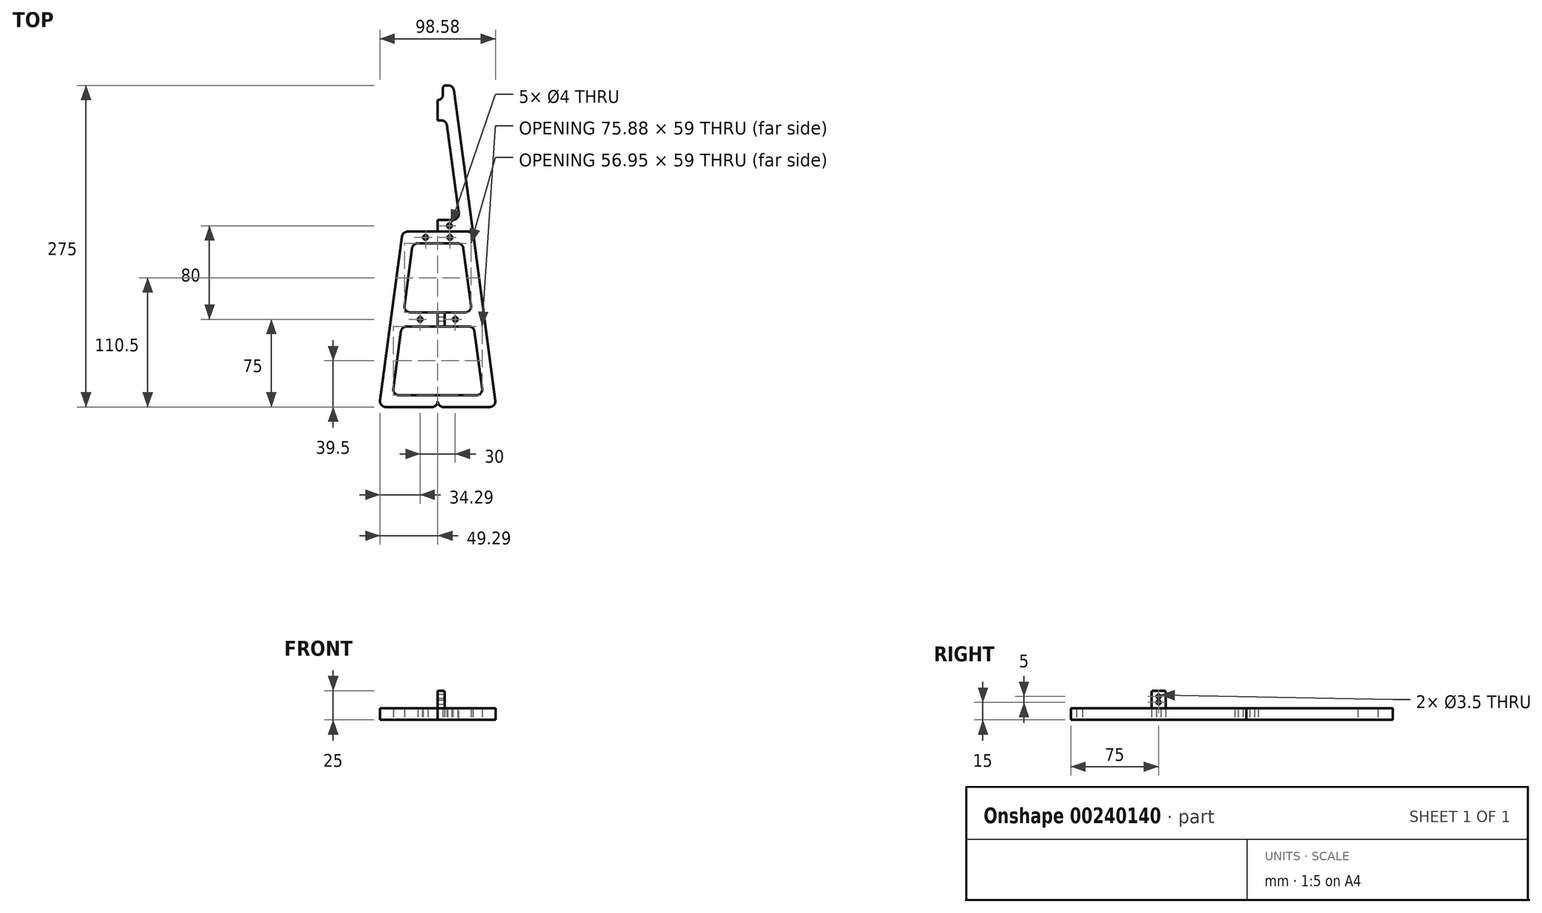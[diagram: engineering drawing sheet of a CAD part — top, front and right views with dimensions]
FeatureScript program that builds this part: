
annotation { "Feature Type Name" : "Feature", "Feature Type Description" : "" }
export const myFeature = defineFeature(function(context is Context, id is Id, definition is map)
    precondition{}
    {
        {
            var Q0;
            Q0=qCreatedBy(makeId("Top.planeOp"),FACE);
            var sketch = newSketch(context, id + "F0", { "sketchPlane" : qUnion([Q0])});
            skLineSegment(sketch, "E0.top", {"start": v(0, 75) * mm, "end": v(-30, 75) * mm});
            skPoint(sketch, "E0.middle", {"position": v(0, 0) * mm});
            skLineSegment(sketch, "E1", {"start": v(-30, 75) * mm, "end": v(-50, -75) * mm});
            skPoint(sketch, "E0.right.end.orphan", {"position": v(-50, 75) * mm});
            skPoint(sketch, "E0.left.end.orphan", {"position": v(50, 75) * mm});
            skLineSegment(sketch, "E2", {"start": v(0, 0) * mm, "end": v(0, 6) * mm});
            skLineSegment(sketch, "E3", {"start": v(-50, -75) * mm, "end": v(-40, -75) * mm});
            skLineSegment(sketch, "E4", {"start": v(-30, 75) * mm, "end": v(-20, 75) * mm});
            skLineSegment(sketch, "E5", {"start": v(0, 75) * mm, "end": v(0, 65) * mm});
            skLineSegment(sketch, "E6", {"start": v(0, 65) * mm, "end": v(-21.33, 65) * mm});
            skLineSegment(sketch, "E7", {"start": v(0, -75) * mm, "end": v(0, -65) * mm});
            skLineSegment(sketch, "E8", {"start": v(0, -65) * mm, "end": v(-38.67, -65) * mm});
            skLineSegment(sketch, "E9", {"start": v(0, 6) * mm, "end": v(-29.2, 6) * mm});
            skLineSegment(sketch, "E10", {"start": v(0, 0) * mm, "end": v(0, -6) * mm});
            skLineSegment(sketch, "E11", {"start": v(0, -6) * mm, "end": v(-30.8, -6) * mm});
            skLineSegment(sketch, "E12.trimOffspring", {"start": v(-30.8, -6) * mm, "end": v(-38.67, -65) * mm});
            skLineSegment(sketch, "E13", {"start": v(-21.33, 65) * mm, "end": v(-29.2, 6) * mm});
            skLineSegment(sketch, "E14.trimOffspring", {"start": v(0, -75) * mm, "end": v(-50, -75) * mm});
            skPoint(sketch, "E0.bottom.start.orphan", {"position": v(50, -75) * mm});
            skCircle(sketch, "E15", {"center": v(-15, 0) * mm, "radius": 2 * mm});
            skLineSegment(sketch, "E16", {"start": v(0, 65) * mm, "end": v(0, 70) * mm});
            skCircle(sketch, "E17", {"center": v(-10.41, 70) * mm, "radius": 2 * mm});
            skSolve(sketch);
        }
        {
            var Q0;
            Q0=qSketchRegion(id+"F0",true);
            extrude(context, id + "F1", {"entities" : qUnion([Q0]), "depth" : 10 * mm});
        }
        {
            var Q0;
            Q0=makeQuery(id+"F1.opExtrude","SWEPT_EDGE",EDGE,{"disambiguationData":[OSD([sQuery(id+"F0.wireOp",EDGE,"E6"),sQuery(id+"F0.wireOp",EDGE,"E13")])]});
            var Q1;
            Q1=makeQuery(id+"F1.opExtrude","SWEPT_EDGE",EDGE,{"disambiguationData":[OSD([sQuery(id+"F0.wireOp",EDGE,"E11"),sQuery(id+"F0.wireOp",EDGE,"E12.trimOffspring")])]});
            var Q2;
            Q2=makeQuery(id+"F1.opExtrude","SWEPT_EDGE",EDGE,{"disambiguationData":[OSD([sQuery(id+"F0.wireOp",EDGE,"E9"),sQuery(id+"F0.wireOp",EDGE,"E13")])]});
            var Q3;
            Q3=makeQuery(id+"F1.opExtrude","SWEPT_EDGE",EDGE,{"disambiguationData":[OSD([sQuery(id+"F0.wireOp",EDGE,"E8"),sQuery(id+"F0.wireOp",EDGE,"E12.trimOffspring")])]});
            var Q4;
            Q4=makeQuery(id+"F1.opExtrude","SWEPT_EDGE",EDGE,{"disambiguationData":[OSD([sQuery(id+"F0.wireOp",EDGE,"E1"),sQuery(id+"F0.wireOp",EDGE,"E14.trimOffspring")])]});
            fillet(context, id + "F2", {"entities" : qUnion([Q0, Q1, Q2, Q3, Q4]), "radius" : 5 * mm, "tangentPropagation" : true, "allowEdgeOverflow" : false});
        }
        {
            var Q0;
            Q0=makeQuery(id+"F1.opExtrude","SWEPT_BODY",BODY,{"disambiguationData":[OSD([sQuery(id+"F0.wireOp",EDGE,"E0.top"),sQuery(id+"F0.wireOp",EDGE,"E1"),sQuery(id+"F0.wireOp",EDGE,"E2"),sQuery(id+"F0.wireOp",EDGE,"E4"),sQuery(id+"F0.wireOp",EDGE,"E5"),sQuery(id+"F0.wireOp",EDGE,"E6"),sQuery(id+"F0.wireOp",EDGE,"E7"),sQuery(id+"F0.wireOp",EDGE,"E8"),sQuery(id+"F0.wireOp",EDGE,"E9"),sQuery(id+"F0.wireOp",EDGE,"E10"),sQuery(id+"F0.wireOp",EDGE,"E11"),sQuery(id+"F0.wireOp",EDGE,"E12.trimOffspring"),sQuery(id+"F0.wireOp",EDGE,"E13"),sQuery(id+"F0.wireOp",EDGE,"E14.trimOffspring"),sQuery(id+"F0.wireOp",EDGE,"E15"),sQuery(id+"F0.wireOp",EDGE,"E16"),sQuery(id+"F0.wireOp",EDGE,"E17")])]});
            var Q1;
            Q1=qCreatedBy(makeId("Right.planeOp"),FACE);
            mirror(context, id + "F3", {"operationType" : NewBodyOperationType.ADD, "entities" : qUnion([Q0]), "mirrorPlane" : qUnion([Q1])});
        }
        {
            var Q0;
            Q0=qCreatedBy(makeId("Top.planeOp"),FACE);
            var sketch = newSketch(context, id + "F4", { "sketchPlane" : qUnion([Q0])});
            skLineSegment(sketch, "E18", {"start": v(0, 0) * mm, "end": v(40, 0) * mm});
            skLineSegment(sketch, "E19", {"start": v(0, 75) * mm, "end": v(30, 75) * mm});
            skLineSegment(sketch, "E20", {"start": v(0, 75) * mm, "end": v(0, 85) * mm});
            skLineSegment(sketch, "E21", {"start": v(4.5, 200) * mm, "end": v(13.33, 200) * mm});
            skLineSegment(sketch, "E22", {"start": v(30, 75) * mm, "end": v(13.33, 200) * mm});
            skArc(sketch, "E23", {"start": v(0, 187.5) * mm, "mid": v(3.18, 188.82) * mm, "end": v(4.5, 192) * mm});
            skLineSegment(sketch, "E24", {"start": v(4.5, 200) * mm, "end": v(4.5, 192) * mm});
            skLineSegment(sketch, "E25", {"start": v(0, 75) * mm, "end": v(0, 80) * mm});
            skCircle(sketch, "E26", {"center": v(10, 80) * mm, "radius": 2 * mm});
            skLineSegment(sketch, "E27", {"start": v(0, 75) * mm, "end": v(10, 75) * mm});
            skLineSegment(sketch, "E28", {"start": v(10, 85) * mm, "end": v(18.67, 85) * mm});
            skLineSegment(sketch, "E29", {"start": v(18.67, 85) * mm, "end": v(10, 150) * mm});
            skLineSegment(sketch, "E30", {"start": v(10, 85) * mm, "end": v(0, 85) * mm});
            skLineSegment(sketch, "E31", {"start": v(18.67, 85) * mm, "end": v(7.31, 170.17) * mm});
            skLineSegment(sketch, "E32", {"start": v(7.31, 170.17) * mm, "end": v(0, 170.17) * mm});
            skLineSegment(sketch, "E33.trimOffspring", {"start": v(0, 170.17) * mm, "end": v(0, 187.5) * mm});
            skSolve(sketch);
        }
        {
            var Q0;
            Q0=qSketchRegion(id+"F4",true);
            extrude(context, id + "F5", {"entities" : qUnion([Q0]), "depth" : 10 * mm});
        }
        {
            var Q0;
            Q0=makeQuery(id+"F5.opExtrude","SWEPT_BODY",BODY,{"disambiguationData":[OSD([sQuery(id+"F4.wireOp",EDGE,"E19"),sQuery(id+"F4.wireOp",EDGE,"E20"),sQuery(id+"F4.wireOp",EDGE,"E21"),sQuery(id+"F4.wireOp",EDGE,"E22"),sQuery(id+"F4.wireOp",EDGE,"E23"),sQuery(id+"F4.wireOp",EDGE,"E24"),sQuery(id+"F4.wireOp",EDGE,"E25"),sQuery(id+"F4.wireOp",EDGE,"E26"),sQuery(id+"F4.wireOp",EDGE,"E27"),sQuery(id+"F4.wireOp",EDGE,"E28"),sQuery(id+"F4.wireOp",EDGE,"E30"),sQuery(id+"F4.wireOp",EDGE,"E31"),sQuery(id+"F4.wireOp",EDGE,"E32"),sQuery(id+"F4.wireOp",EDGE,"E33.trimOffspring")])]});
            var Q1;
            Q1=qCreatedBy(makeId("Right.planeOp"),FACE);
            mirror(context, id + "F6", {"entities" : qUnion([Q0]), "mirrorPlane" : qUnion([Q1])});
        }
        {
            var Q0;
            Q0=makeQuery(id+"F6.opPattern","COPY",EDGE,{"derivedFrom":makeQuery(id+"F5.opExtrude","SWEPT_EDGE",EDGE,{"disambiguationData":[OSD([sQuery(id+"F4.wireOp",EDGE,"E31"),sQuery(id+"F4.wireOp",EDGE,"E32")])]}),"instanceName":"1"});
            var Q1;
            Q1=makeQuery(id+"F5.opExtrude","SWEPT_EDGE",EDGE,{"disambiguationData":[OSD([sQuery(id+"F4.wireOp",EDGE,"E31"),sQuery(id+"F4.wireOp",EDGE,"E32")])]});
            var Q2;
            Q2=makeQuery(id+"F6.opPattern","COPY",EDGE,{"derivedFrom":makeQuery(id+"F5.opExtrude","SWEPT_EDGE",EDGE,{"disambiguationData":[OSD([sQuery(id+"F4.wireOp",EDGE,"E28"),sQuery(id+"F4.wireOp",EDGE,"E31")])]}),"instanceName":"1"});
            var Q3;
            Q3=makeQuery(id+"F5.opExtrude","SWEPT_EDGE",EDGE,{"disambiguationData":[OSD([sQuery(id+"F4.wireOp",EDGE,"E28"),sQuery(id+"F4.wireOp",EDGE,"E31")])]});
            var Q4;
            Q4=makeQuery(id+"F6.opPattern","COPY",EDGE,{"derivedFrom":makeQuery(id+"F5.opExtrude","SWEPT_EDGE",EDGE,{"disambiguationData":[OSD([sQuery(id+"F4.wireOp",EDGE,"E21"),sQuery(id+"F4.wireOp",EDGE,"E22")])]}),"instanceName":"1"});
            var Q5;
            Q5=makeQuery(id+"F5.opExtrude","SWEPT_EDGE",EDGE,{"disambiguationData":[OSD([sQuery(id+"F4.wireOp",EDGE,"E21"),sQuery(id+"F4.wireOp",EDGE,"E22")])]});
            fillet(context, id + "F7", {"entities" : qUnion([Q0, Q1, Q2, Q3, Q4, Q5]), "radius" : 5 * mm, "tangentPropagation" : true, "allowEdgeOverflow" : false});
        }
        {
            var Q0;
            Q0=makeQuery(id+"F5.opExtrude","SWEPT_EDGE",EDGE,{"disambiguationData":[OSD([sQuery(id+"F4.wireOp",EDGE,"E21"),sQuery(id+"F4.wireOp",EDGE,"E24")])]});
            var Q1;
            Q1=makeQuery(id+"F6.opPattern","COPY",EDGE,{"derivedFrom":makeQuery(id+"F5.opExtrude","SWEPT_EDGE",EDGE,{"disambiguationData":[OSD([sQuery(id+"F4.wireOp",EDGE,"E21"),sQuery(id+"F4.wireOp",EDGE,"E24")])]}),"instanceName":"1"});
            fillet(context, id + "F8", {"entities" : qUnion([Q0, Q1]), "radius" : 2 * mm, "tangentPropagation" : true, "allowEdgeOverflow" : false});
        }
        {
            var Q0;
            Q0=qCreatedBy(makeId("Top.planeOp"),FACE);
            var sketch = newSketch(context, id + "F9", { "sketchPlane" : qUnion([Q0])});
            skLineSegment(sketch, "E34", {"start": v(0, 0) * mm, "end": v(0, 6) * mm});
            skLineSegment(sketch, "E35", {"start": v(0, 6) * mm, "end": v(-6, 6) * mm});
            skLineSegment(sketch, "E36", {"start": v(-6, 6) * mm, "end": v(-6, -6) * mm});
            skLineSegment(sketch, "E37", {"start": v(-6, -6) * mm, "end": v(0, -6) * mm});
            skLineSegment(sketch, "E38", {"start": v(0, -6) * mm, "end": v(0, 0) * mm});
            skSolve(sketch);
        }
        {
            var Q0;
            Q0=qSketchRegion(id+"F9",true);
            extrude(context, id + "F10", {"entities" : qUnion([Q0]), "operationType" : NewBodyOperationType.ADD, "depth" : 25 * mm});
        }
        {
            var Q0;
            Q0=makeQuery(id+"F10.opExtrude","SWEPT_EDGE",EDGE,{"disambiguationData":[OSD([sQuery(id+"F9.wireOp",EDGE,"E36"),sQuery(id+"F9.wireOp",EDGE,"E37")])]});
            var Q1;
            Q1=makeQuery(id+"F10.opExtrude","CAP_EDGE",EDGE,{"disambiguationData":[OSD([sQuery(id+"F9.wireOp",EDGE,"E36")])],"isStart":false});
            var Q2;
            Q2=makeQuery(id+"F10.opExtrude","CAP_EDGE",EDGE,{"disambiguationData":[OSD([sQuery(id+"F9.wireOp",EDGE,"E37")])],"isStart":false});
            var Q3;
            Q3=makeQuery(id+"F10.opExtrude","SWEPT_EDGE",EDGE,{"disambiguationData":[OSD([sQuery(id+"F9.wireOp",EDGE,"E35"),sQuery(id+"F9.wireOp",EDGE,"E36")])]});
            var Q4;
            Q4=makeQuery(id+"F10.opExtrude","CAP_EDGE",EDGE,{"disambiguationData":[OSD([sQuery(id+"F9.wireOp",EDGE,"E35")])],"isStart":false});
            fillet(context, id + "F11", {"entities" : qUnion([Q0, Q1, Q2, Q3, Q4]), "radius" : 1.5 * mm, "tangentPropagation" : true, "allowEdgeOverflow" : false});
        }
        {
            var Q0;
            Q0=qCreatedBy(makeId("Right.planeOp"),FACE);
            var sketch = newSketch(context, id + "F12", { "sketchPlane" : qUnion([Q0])});
            skCircle(sketch, "E39", {"center": v(0, 20) * mm, "radius": 1.75 * mm});
            skCircle(sketch, "E40", {"center": v(0, 15) * mm, "radius": 1.75 * mm});
            skSolve(sketch);
        }
        {
            var Q0;
            Q0=qSketchRegion(id+"F12",true);
            extrude(context, id + "F13", {"entities" : qUnion([Q0]), "endBound" : BoundingType.SYMMETRIC, "depth" : 25 * mm});
        }
        {
            var Q0;
            Q0=makeQuery(id+"F13.opExtrude","SWEPT_BODY",BODY,{"disambiguationData":[OSD([sQuery(id+"F12.wireOp",EDGE,"E40")])]});
            var Q1;
            Q1=makeQuery(id+"F13.opExtrude","SWEPT_BODY",BODY,{"disambiguationData":[OSD([sQuery(id+"F12.wireOp",EDGE,"E39")])]});
            var Q2;
            Q2=makeQuery(id+"F1.opExtrude","SWEPT_BODY",BODY,{"disambiguationData":[OSD([sQuery(id+"F0.wireOp",EDGE,"E0.top"),sQuery(id+"F0.wireOp",EDGE,"E1"),sQuery(id+"F0.wireOp",EDGE,"E2"),sQuery(id+"F0.wireOp",EDGE,"E4"),sQuery(id+"F0.wireOp",EDGE,"E5"),sQuery(id+"F0.wireOp",EDGE,"E6"),sQuery(id+"F0.wireOp",EDGE,"E7"),sQuery(id+"F0.wireOp",EDGE,"E8"),sQuery(id+"F0.wireOp",EDGE,"E9"),sQuery(id+"F0.wireOp",EDGE,"E10"),sQuery(id+"F0.wireOp",EDGE,"E11"),sQuery(id+"F0.wireOp",EDGE,"E12.trimOffspring"),sQuery(id+"F0.wireOp",EDGE,"E13"),sQuery(id+"F0.wireOp",EDGE,"E14.trimOffspring"),sQuery(id+"F0.wireOp",EDGE,"E15"),sQuery(id+"F0.wireOp",EDGE,"E16"),sQuery(id+"F0.wireOp",EDGE,"E17")])]});
            booleanBodies(context, id + "F14", {"operationType" : BooleanOperationType.SUBTRACTION, "tools" : qUnion([Q0, Q1]), "targets" : qUnion([Q2])});
        }
        {
            var Q0;
            Q0=qCreatedBy(makeId("Top.planeOp"),FACE);
            var sketch = newSketch(context, id + "F15", { "sketchPlane" : qUnion([Q0])});
            skLineSegment(sketch, "E41.bottom", {"start": v(15, 65) * mm, "end": v(-15, 65) * mm});
            skLineSegment(sketch, "E41.top", {"start": v(15, 85) * mm, "end": v(-15, 85) * mm});
            skLineSegment(sketch, "E41.left", {"start": v(15, 65) * mm, "end": v(15, 85) * mm});
            skLineSegment(sketch, "E41.right", {"start": v(-15, 65) * mm, "end": v(-15, 85) * mm});
            skPoint(sketch, "E41.middle", {"position": v(0, 75) * mm});
            skLineSegment(sketch, "E42", {"start": v(0, 75) * mm, "end": v(0, 85) * mm});
            skLineSegment(sketch, "E43", {"start": v(0, 85) * mm, "end": v(0, 65) * mm});
            skLineSegment(sketch, "E44", {"start": v(0, 65) * mm, "end": v(-6, 65) * mm});
            skLineSegment(sketch, "E45", {"start": v(-6, 65) * mm, "end": v(-6, 85) * mm});
            skLineSegment(sketch, "E46", {"start": v(-6, 85) * mm, "end": v(0, 85) * mm});
            skSolve(sketch);
        }
        {
            var Q0;
            Q0=qSketchRegion(id+"F15",true);
            extrude(context, id + "F16", {"entities" : qUnion([Q0]), "depth" : 10 * mm});
        }
        {
            var Q0;
            Q0=qCreatedBy(makeId("Top.planeOp"),FACE);
            var sketch = newSketch(context, id + "F17", { "sketchPlane" : qUnion([Q0])});
            skLineSegment(sketch, "E47", {"start": v(0, 65) * mm, "end": v(0, 85) * mm});
            skLineSegment(sketch, "E48", {"start": v(0, 85) * mm, "end": v(-6, 85) * mm});
            skLineSegment(sketch, "E49", {"start": v(-6, 85) * mm, "end": v(-6, 65) * mm});
            skLineSegment(sketch, "E50", {"start": v(-6, 65) * mm, "end": v(0, 65) * mm});
            skSolve(sketch);
        }
        {
            var Q0;
            Q0=qSketchRegion(id+"F17",true);
            extrude(context, id + "F18", {"entities" : qUnion([Q0]), "depth" : 25 * mm});
        }
        {
            var Q0;
            Q0=makeQuery(id+"F16.opExtrude","SWEPT_BODY",BODY,{"disambiguationData":[OSD([sQuery(id+"F15.wireOp",EDGE,"E41.bottom"),sQuery(id+"F15.wireOp",EDGE,"E41.top"),sQuery(id+"F15.wireOp",EDGE,"E41.left"),sQuery(id+"F15.wireOp",EDGE,"E41.right"),sQuery(id+"F15.wireOp",EDGE,"E44"),sQuery(id+"F15.wireOp",EDGE,"E46")])]});
            var Q1;
            Q1=makeQuery(id+"F18.opExtrude","SWEPT_BODY",BODY,{"disambiguationData":[OSD([sQuery(id+"F17.wireOp",EDGE,"E47"),sQuery(id+"F17.wireOp",EDGE,"E48"),sQuery(id+"F17.wireOp",EDGE,"E49"),sQuery(id+"F17.wireOp",EDGE,"E50")])]});
            booleanBodies(context, id + "F19", {"operationType" : BooleanOperationType.UNION, "tools" : qUnion([Q0, Q1])});
        }
        {
            var Q0;
            Q0=makeQuery(id+"F16.opExtrude","SWEPT_BODY",BODY,{"disambiguationData":[OSD([sQuery(id+"F15.wireOp",EDGE,"E41.bottom"),sQuery(id+"F15.wireOp",EDGE,"E41.top"),sQuery(id+"F15.wireOp",EDGE,"E41.left"),sQuery(id+"F15.wireOp",EDGE,"E41.right"),sQuery(id+"F15.wireOp",EDGE,"E44"),sQuery(id+"F15.wireOp",EDGE,"E46")])]});
            transform(context, id + "F20", {"entities" : qUnion([Q0]), "transformType" : TransformType.TRANSLATION_3D, "dx" : 0 * mm, "dy" : 0 * mm, "dz" : 10 * mm, "makeCopy" : false});
        }
        {
            var Q0;
            Q0=qCreatedBy(makeId("Top.planeOp"),FACE);
            var sketch = newSketch(context, id + "F21", { "sketchPlane" : qUnion([Q0])});
            skCircle(sketch, "E51", {"center": v(-10, 80) * mm, "radius": 2 * mm});
            skCircle(sketch, "E52", {"center": v(10, 80) * mm, "radius": 2 * mm});
            skCircle(sketch, "E53", {"center": v(-10.4, 70) * mm, "radius": 2 * mm});
            skCircle(sketch, "E54", {"center": v(10.4, 70) * mm, "radius": 2 * mm});
            skSolve(sketch);
        }
        {
            var Q0;
            Q0=qSketchRegion(id+"F21",true);
            extrude(context, id + "F22", {"entities" : qUnion([Q0]), "depth" : 30 * mm});
        }
        {
            var Q0;
            Q0=makeQuery(id+"F22.opExtrude","SWEPT_BODY",BODY,{"disambiguationData":[OSD([sQuery(id+"F21.wireOp",EDGE,"E54")])]});
            var Q1;
            Q1=makeQuery(id+"F22.opExtrude","SWEPT_BODY",BODY,{"disambiguationData":[OSD([sQuery(id+"F21.wireOp",EDGE,"E53")])]});
            var Q2;
            Q2=makeQuery(id+"F22.opExtrude","SWEPT_BODY",BODY,{"disambiguationData":[OSD([sQuery(id+"F21.wireOp",EDGE,"E52")])]});
            var Q3;
            Q3=makeQuery(id+"F22.opExtrude","SWEPT_BODY",BODY,{"disambiguationData":[OSD([sQuery(id+"F21.wireOp",EDGE,"E51")])]});
            var Q4;
            Q4=makeQuery(id+"F16.opExtrude","SWEPT_BODY",BODY,{"disambiguationData":[OSD([sQuery(id+"F15.wireOp",EDGE,"E41.bottom"),sQuery(id+"F15.wireOp",EDGE,"E41.top"),sQuery(id+"F15.wireOp",EDGE,"E41.left"),sQuery(id+"F15.wireOp",EDGE,"E41.right"),sQuery(id+"F15.wireOp",EDGE,"E44"),sQuery(id+"F15.wireOp",EDGE,"E46")])]});
            booleanBodies(context, id + "F23", {"operationType" : BooleanOperationType.SUBTRACTION, "tools" : qUnion([Q0, Q1, Q2, Q3]), "targets" : qUnion([Q4])});
        }
        {
            var Q0;
            Q0=qCreatedBy(makeId("Right.planeOp"),FACE);
            var sketch = newSketch(context, id + "F24", { "sketchPlane" : qUnion([Q0])});
            skCircle(sketch, "E55", {"center": v(80, 27.23) * mm, "radius": 2 * mm});
            skCircle(sketch, "E56", {"center": v(70, 27.23) * mm, "radius": 2 * mm});
            skSolve(sketch);
        }
        {
            var Q0;
            Q0=qSketchRegion(id+"F24",true);
            extrude(context, id + "F25", {"entities" : qUnion([Q0]), "endBound" : BoundingType.SYMMETRIC, "depth" : 25 * mm});
        }
        {
            var Q0;
            Q0=makeQuery(id+"F25.opExtrude","SWEPT_BODY",BODY,{"disambiguationData":[OSD([sQuery(id+"F24.wireOp",EDGE,"E56")])]});
            var Q1;
            Q1=makeQuery(id+"F25.opExtrude","SWEPT_BODY",BODY,{"disambiguationData":[OSD([sQuery(id+"F24.wireOp",EDGE,"E55")])]});
            var Q2;
            Q2=makeQuery(id+"F16.opExtrude","SWEPT_BODY",BODY,{"disambiguationData":[OSD([sQuery(id+"F15.wireOp",EDGE,"E41.bottom"),sQuery(id+"F15.wireOp",EDGE,"E41.top"),sQuery(id+"F15.wireOp",EDGE,"E41.left"),sQuery(id+"F15.wireOp",EDGE,"E41.right"),sQuery(id+"F15.wireOp",EDGE,"E44"),sQuery(id+"F15.wireOp",EDGE,"E46")])]});
            booleanBodies(context, id + "F26", {"operationType" : BooleanOperationType.SUBTRACTION, "tools" : qUnion([Q0, Q1]), "targets" : qUnion([Q2])});
        }
        {
            var Q0;
            Q0=makeQuery(id+"F18.opExtrude","SWEPT_EDGE",EDGE,{"disambiguationData":[OSD([sQuery(id+"F17.wireOp",EDGE,"E49"),sQuery(id+"F17.wireOp",EDGE,"E50")])]});
            var Q1;
            Q1=makeQuery(id+"F18.opExtrude","CAP_EDGE",EDGE,{"disambiguationData":[OSD([sQuery(id+"F17.wireOp",EDGE,"E50")])],"isStart":false});
            var Q2;
            {var subQ0=sQuery(id+"F15.wireOp",EDGE,"E44");var subQ1=sQuery(id+"F15.wireOp",EDGE,"E41.bottom");var subQ2=sQuery(id+"F15.wireOp",EDGE,"E41.right");Q2=makeQuery(id+"F19.opBoolean","SPLIT",EDGE,{"disambiguationData":[TD([makeQuery(id+"F16.opExtrude","SWEPT_FACE",FACE,{"disambiguationData":[OSD([subQ2])]})])],"derivedFrom":makeQuery(id+"F16.opExtrude","CAP_EDGE",EDGE,{"disambiguationData":[OSD([subQ1,subQ0])],"isStart":false})});}
            var Q3;
            Q3=makeQuery(id+"F16.opExtrude","SWEPT_EDGE",EDGE,{"disambiguationData":[OSD([sQuery(id+"F15.wireOp",EDGE,"E41.bottom"),sQuery(id+"F15.wireOp",EDGE,"E41.right")])]});
            var Q4;
            {var subQ0=sQuery(id+"F15.wireOp",EDGE,"E41.left");var subQ1=sQuery(id+"F15.wireOp",EDGE,"E44");var subQ2=sQuery(id+"F15.wireOp",EDGE,"E41.bottom");Q4=makeQuery(id+"F19.opBoolean","SPLIT",EDGE,{"disambiguationData":[TD([makeQuery(id+"F16.opExtrude","SWEPT_FACE",FACE,{"disambiguationData":[OSD([subQ0])]})])],"derivedFrom":makeQuery(id+"F16.opExtrude","CAP_EDGE",EDGE,{"disambiguationData":[OSD([subQ2,subQ1])],"isStart":false})});}
            var Q5;
            Q5=makeQuery(id+"F16.opExtrude","SWEPT_EDGE",EDGE,{"disambiguationData":[OSD([sQuery(id+"F15.wireOp",EDGE,"E41.bottom"),sQuery(id+"F15.wireOp",EDGE,"E41.left")])]});
            var Q6;
            Q6=makeQuery(id+"F16.opExtrude","CAP_EDGE",EDGE,{"disambiguationData":[OSD([sQuery(id+"F15.wireOp",EDGE,"E41.left")])],"isStart":false});
            var Q7;
            Q7=makeQuery(id+"F16.opExtrude","CAP_EDGE",EDGE,{"disambiguationData":[OSD([sQuery(id+"F15.wireOp",EDGE,"E41.right")])],"isStart":false});
            var Q8;
            Q8=makeQuery(id+"F18.opExtrude","CAP_EDGE",EDGE,{"disambiguationData":[OSD([sQuery(id+"F17.wireOp",EDGE,"E49")])],"isStart":false});
            var Q9;
            {var subQ0=sQuery(id+"F15.wireOp",EDGE,"E41.right");var subQ1=sQuery(id+"F15.wireOp",EDGE,"E46");var subQ2=sQuery(id+"F15.wireOp",EDGE,"E41.top");Q9=makeQuery(id+"F19.opBoolean","SPLIT",EDGE,{"disambiguationData":[TD([makeQuery(id+"F16.opExtrude","SWEPT_FACE",FACE,{"disambiguationData":[OSD([subQ0])]})])],"derivedFrom":makeQuery(id+"F16.opExtrude","CAP_EDGE",EDGE,{"disambiguationData":[OSD([subQ2,subQ1])],"isStart":false})});}
            var Q10;
            Q10=makeQuery(id+"F16.opExtrude","SWEPT_EDGE",EDGE,{"disambiguationData":[OSD([sQuery(id+"F15.wireOp",EDGE,"E41.top"),sQuery(id+"F15.wireOp",EDGE,"E41.right")])]});
            var Q11;
            Q11=makeQuery(id+"F18.opExtrude","SWEPT_EDGE",EDGE,{"disambiguationData":[OSD([sQuery(id+"F17.wireOp",EDGE,"E48"),sQuery(id+"F17.wireOp",EDGE,"E49")])]});
            var Q12;
            Q12=makeQuery(id+"F18.opExtrude","CAP_EDGE",EDGE,{"disambiguationData":[OSD([sQuery(id+"F17.wireOp",EDGE,"E48")])],"isStart":false});
            var Q13;
            {var subQ0=sQuery(id+"F15.wireOp",EDGE,"E41.left");var subQ1=sQuery(id+"F15.wireOp",EDGE,"E46");var subQ2=sQuery(id+"F15.wireOp",EDGE,"E41.top");Q13=makeQuery(id+"F19.opBoolean","SPLIT",EDGE,{"disambiguationData":[TD([makeQuery(id+"F16.opExtrude","SWEPT_FACE",FACE,{"disambiguationData":[OSD([subQ0])]})])],"derivedFrom":makeQuery(id+"F16.opExtrude","CAP_EDGE",EDGE,{"disambiguationData":[OSD([subQ2,subQ1])],"isStart":false})});}
            var Q14;
            Q14=makeQuery(id+"F16.opExtrude","SWEPT_EDGE",EDGE,{"disambiguationData":[OSD([sQuery(id+"F15.wireOp",EDGE,"E41.top"),sQuery(id+"F15.wireOp",EDGE,"E41.left")])]});
            fillet(context, id + "F27", {"entities" : qUnion([Q0, Q1, Q2, Q3, Q4, Q5, Q6, Q7, Q8, Q9, Q10, Q11, Q12, Q13, Q14]), "radius" : 2 * mm, "tangentPropagation" : true, "allowEdgeOverflow" : false});
        }
        {
            var Q0;
            Q0=qCreatedBy(makeId("Right.planeOp"),FACE);
            var sketch = newSketch(context, id + "F28", { "sketchPlane" : qUnion([Q0])});
            skLineSegment(sketch, "E57", {"start": v(0, 0) * mm, "end": v(0, 10) * mm});
            skLineSegment(sketch, "E58", {"start": v(0, 10) * mm, "end": v(6, 10) * mm});
            skLineSegment(sketch, "E59", {"start": v(6, 10) * mm, "end": v(6, 25) * mm});
            skLineSegment(sketch, "E60", {"start": v(-6, 25) * mm, "end": v(-6, 10) * mm});
            skLineSegment(sketch, "E61", {"start": v(-6, 10) * mm, "end": v(0, 10) * mm});
            skLineSegment(sketch, "E62", {"start": v(75, 10) * mm, "end": v(75, 20) * mm});
            skLineSegment(sketch, "E63", {"start": v(75, 20) * mm, "end": v(85, 20) * mm});
            skLineSegment(sketch, "E64", {"start": v(85, 20) * mm, "end": v(85, 35) * mm});
            skLineSegment(sketch, "E65", {"start": v(65, 35) * mm, "end": v(65, 20) * mm});
            skLineSegment(sketch, "E66", {"start": v(65, 20) * mm, "end": v(75, 20) * mm});
            skLineSegment(sketch, "E67", {"start": v(-6, 10) * mm, "end": v(-6, 25) * mm});
            skLineSegment(sketch, "E68", {"start": v(75, 120) * mm, "end": v(85, 120) * mm});
            skLineSegment(sketch, "E69", {"start": v(85, 35) * mm, "end": v(85, 120) * mm});
            skLineSegment(sketch, "E70", {"start": v(85, 120) * mm, "end": v(75, 120) * mm});
            skLineSegment(sketch, "E71", {"start": v(6, 25) * mm, "end": v(65, 35) * mm});
            skLineSegment(sketch, "E72", {"start": v(-6, 25) * mm, "end": v(75, 120) * mm});
            skLineSegment(sketch, "E73", {"start": v(23.92, 44.68) * mm, "end": v(75, 104.59) * mm});
            skLineSegment(sketch, "E74", {"start": v(23.92, 44.68) * mm, "end": v(17.44, 37.08) * mm});
            skLineSegment(sketch, "E75", {"start": v(75, 45) * mm, "end": v(64.16, 45) * mm});
            skLineSegment(sketch, "E76", {"start": v(51.92, 42.93) * mm, "end": v(17.44, 37.08) * mm});
            skLineSegment(sketch, "E77", {"start": v(51.92, 42.93) * mm, "end": v(64.16, 45) * mm});
            skPoint(sketch, "E78.orphan", {"position": v(75, 35) * mm});
            skPoint(sketch, "E79.start.orphan", {"position": v(75, 110) * mm});
            skLineSegment(sketch, "E80", {"start": v(75, 104.59) * mm, "end": v(75, 45) * mm});
            skCircle(sketch, "E81", {"center": v(80, 110) * mm, "radius": 2 * mm});
            skCircle(sketch, "E82", {"center": v(80, 95) * mm, "radius": 2 * mm});
            skPoint(sketch, "E83.end.orphan", {"position": v(80, 120) * mm});
            skSolve(sketch);
        }
        {
            var Q0;
            Q0=qSketchRegion(id+"F28",true);
            extrude(context, id + "F29", {"entities" : qUnion([Q0]), "depth" : 8 * mm});
        }
        {
            var Q0;
            Q0=makeQuery(id+"F29.opExtrude","SWEPT_EDGE",EDGE,{"disambiguationData":[OSD([sQuery(id+"F28.wireOp",EDGE,"E73"),sQuery(id+"F28.wireOp",EDGE,"E80")])]});
            var Q1;
            Q1=makeQuery(id+"F29.opExtrude","SWEPT_EDGE",EDGE,{"disambiguationData":[OSD([sQuery(id+"F28.wireOp",EDGE,"E75"),sQuery(id+"F28.wireOp",EDGE,"E80")])]});
            var Q2;
            Q2=makeQuery(id+"F29.opExtrude","SWEPT_EDGE",EDGE,{"disambiguationData":[OSD([sQuery(id+"F28.wireOp",EDGE,"E74"),sQuery(id+"F28.wireOp",EDGE,"E76")])]});
            var Q3;
            Q3=makeQuery(id+"F29.opExtrude","SWEPT_EDGE",EDGE,{"disambiguationData":[OSD([sQuery(id+"F28.wireOp",EDGE,"E65"),sQuery(id+"F28.wireOp",EDGE,"E71")])]});
            var Q4;
            Q4=makeQuery(id+"F29.opExtrude","SWEPT_EDGE",EDGE,{"disambiguationData":[OSD([sQuery(id+"F28.wireOp",EDGE,"E59"),sQuery(id+"F28.wireOp",EDGE,"E71")])]});
            var Q5;
            Q5=makeQuery(id+"F29.opExtrude","SWEPT_EDGE",EDGE,{"disambiguationData":[OSD([sQuery(id+"F28.wireOp",EDGE,"E67"),sQuery(id+"F28.wireOp",EDGE,"E72")])]});
            fillet(context, id + "F30", {"entities" : qUnion([Q0, Q1, Q2, Q3, Q4, Q5]), "radius" : 2 * mm, "tangentPropagation" : true, "allowEdgeOverflow" : false});
        }
        {
            var Q0;
            Q0=makeQuery(id+"F29.opExtrude","CAP_EDGE",EDGE,{"disambiguationData":[OSD([sQuery(id+"F28.wireOp",EDGE,"E73"),sQuery(id+"F28.wireOp",EDGE,"E74")])],"isStart":false});
            var Q1;
            Q1=makeQuery(id+"F29.opExtrude","CAP_EDGE",EDGE,{"disambiguationData":[OSD([sQuery(id+"F28.wireOp",EDGE,"E72")])],"isStart":false});
            var Q2;
            Q2=makeQuery(id+"F29.opExtrude","CAP_EDGE",EDGE,{"disambiguationData":[OSD([sQuery(id+"F28.wireOp",EDGE,"E71")])],"isStart":false});
            var Q3;
            Q3=makeQuery(id+"F29.opExtrude","CAP_EDGE",EDGE,{"disambiguationData":[OSD([sQuery(id+"F28.wireOp",EDGE,"E64"),sQuery(id+"F28.wireOp",EDGE,"E69")])],"isStart":false});
            fillet(context, id + "F31", {"entities" : qUnion([Q0, Q1, Q2, Q3]), "radius" : 2 * mm, "tangentPropagation" : true, "allowEdgeOverflow" : false});
        }
        {
            var Q0;
            Q0=qCreatedBy(makeId("Right.planeOp"),FACE);
            var sketch = newSketch(context, id + "F32", { "sketchPlane" : qUnion([Q0])});
            skCircle(sketch, "E84", {"center": v(0, 20) * mm, "radius": 1.75 * mm});
            skCircle(sketch, "E85", {"center": v(0, 15) * mm, "radius": 1.75 * mm});
            skCircle(sketch, "E86", {"center": v(70, 27.25) * mm, "radius": 2 * mm});
            skCircle(sketch, "E87", {"center": v(80, 27.25) * mm, "radius": 2 * mm});
            skSolve(sketch);
        }
        {
            var Q0;
            Q0=qSketchRegion(id+"F32",true);
            extrude(context, id + "F33", {"entities" : qUnion([Q0]), "depth" : 25 * mm});
        }
        {
            var Q0;
            Q0=makeQuery(id+"F33.opExtrude","SWEPT_BODY",BODY,{"disambiguationData":[OSD([sQuery(id+"F32.wireOp",EDGE,"E87")])]});
            var Q1;
            Q1=makeQuery(id+"F33.opExtrude","SWEPT_BODY",BODY,{"disambiguationData":[OSD([sQuery(id+"F32.wireOp",EDGE,"E86")])]});
            var Q2;
            Q2=makeQuery(id+"F33.opExtrude","SWEPT_BODY",BODY,{"disambiguationData":[OSD([sQuery(id+"F32.wireOp",EDGE,"E85")])]});
            var Q3;
            Q3=makeQuery(id+"F33.opExtrude","SWEPT_BODY",BODY,{"disambiguationData":[OSD([sQuery(id+"F32.wireOp",EDGE,"E84")])]});
            var Q4;
            Q4=makeQuery(id+"F29.opExtrude","SWEPT_BODY",BODY,{"disambiguationData":[OSD([sQuery(id+"F28.wireOp",EDGE,"E59"),sQuery(id+"F28.wireOp",EDGE,"E61"),sQuery(id+"F28.wireOp",EDGE,"E58"),sQuery(id+"F28.wireOp",EDGE,"E63"),sQuery(id+"F28.wireOp",EDGE,"E64"),sQuery(id+"F28.wireOp",EDGE,"E65"),sQuery(id+"F28.wireOp",EDGE,"E66"),sQuery(id+"F28.wireOp",EDGE,"E67"),sQuery(id+"F28.wireOp",EDGE,"E69"),sQuery(id+"F28.wireOp",EDGE,"E70"),sQuery(id+"F28.wireOp",EDGE,"E71"),sQuery(id+"F28.wireOp",EDGE,"E72"),sQuery(id+"F28.wireOp",EDGE,"E73"),sQuery(id+"F28.wireOp",EDGE,"E74"),sQuery(id+"F28.wireOp",EDGE,"E75"),sQuery(id+"F28.wireOp",EDGE,"E76"),sQuery(id+"F28.wireOp",EDGE,"E77"),sQuery(id+"F28.wireOp",EDGE,"E80"),sQuery(id+"F28.wireOp",EDGE,"E81"),sQuery(id+"F28.wireOp",EDGE,"E82")])]});
            booleanBodies(context, id + "F34", {"operationType" : BooleanOperationType.SUBTRACTION, "tools" : qUnion([Q0, Q1, Q2, Q3]), "targets" : qUnion([Q4])});
        }
        {
            var Q0;
            Q0=makeQuery(id+"F6.opPattern","COPY",BODY,{"derivedFrom":makeQuery(id+"F5.opExtrude","SWEPT_BODY",BODY,{"disambiguationData":[OSD([sQuery(id+"F4.wireOp",EDGE,"E19"),sQuery(id+"F4.wireOp",EDGE,"E20"),sQuery(id+"F4.wireOp",EDGE,"E21"),sQuery(id+"F4.wireOp",EDGE,"E22"),sQuery(id+"F4.wireOp",EDGE,"E23"),sQuery(id+"F4.wireOp",EDGE,"E24"),sQuery(id+"F4.wireOp",EDGE,"E25"),sQuery(id+"F4.wireOp",EDGE,"E26"),sQuery(id+"F4.wireOp",EDGE,"E27"),sQuery(id+"F4.wireOp",EDGE,"E28"),sQuery(id+"F4.wireOp",EDGE,"E30"),sQuery(id+"F4.wireOp",EDGE,"E31"),sQuery(id+"F4.wireOp",EDGE,"E32"),sQuery(id+"F4.wireOp",EDGE,"E33.trimOffspring")])]}),"instanceName":"1"});
            var Q1;
            Q1=makeQuery(id+"F16.opExtrude","SWEPT_BODY",BODY,{"disambiguationData":[OSD([sQuery(id+"F15.wireOp",EDGE,"E41.bottom"),sQuery(id+"F15.wireOp",EDGE,"E41.top"),sQuery(id+"F15.wireOp",EDGE,"E41.left"),sQuery(id+"F15.wireOp",EDGE,"E41.right"),sQuery(id+"F15.wireOp",EDGE,"E44"),sQuery(id+"F15.wireOp",EDGE,"E46")])]});
            var Q2;
            Q2=makeQuery(id+"F29.opExtrude","SWEPT_BODY",BODY,{"disambiguationData":[OSD([sQuery(id+"F28.wireOp",EDGE,"E59"),sQuery(id+"F28.wireOp",EDGE,"E61"),sQuery(id+"F28.wireOp",EDGE,"E58"),sQuery(id+"F28.wireOp",EDGE,"E63"),sQuery(id+"F28.wireOp",EDGE,"E64"),sQuery(id+"F28.wireOp",EDGE,"E65"),sQuery(id+"F28.wireOp",EDGE,"E66"),sQuery(id+"F28.wireOp",EDGE,"E67"),sQuery(id+"F28.wireOp",EDGE,"E69"),sQuery(id+"F28.wireOp",EDGE,"E70"),sQuery(id+"F28.wireOp",EDGE,"E71"),sQuery(id+"F28.wireOp",EDGE,"E72"),sQuery(id+"F28.wireOp",EDGE,"E73"),sQuery(id+"F28.wireOp",EDGE,"E74"),sQuery(id+"F28.wireOp",EDGE,"E75"),sQuery(id+"F28.wireOp",EDGE,"E76"),sQuery(id+"F28.wireOp",EDGE,"E77"),sQuery(id+"F28.wireOp",EDGE,"E80"),sQuery(id+"F28.wireOp",EDGE,"E81"),sQuery(id+"F28.wireOp",EDGE,"E82")])]});
            deleteBodies(context, id + "F35", {"entities" : qUnion([Q0, Q1, Q2])});
        }
        {
            var Q0;
            Q0=qCreatedBy(makeId("Right.planeOp"),FACE);
            var sketch = newSketch(context, id + "F36", { "sketchPlane" : qUnion([Q0])});
            skCircle(sketch, "E88", {"center": v(0, 20) * mm, "radius": 1.75 * mm});
            skCircle(sketch, "E89", {"center": v(0, 15) * mm, "radius": 1.75 * mm});
            skSolve(sketch);
        }
        {
            var Q0;
            Q0 = qSketchRegion(id + "F36", true);
            extrude(context, id + "F37", {"entities" : qUnion([Q0]), "endBound" : BoundingType.SYMMETRIC, "depth" : 25 * mm});
        }
        {
            var Q0;
            Q0=qCreatedBy(makeId("Top.planeOp"),FACE);
            var sketch = newSketch(context, id + "F38", { "sketchPlane" : qUnion([Q0])});
            skLineSegment(sketch, "E90", {"start": v(0, 0) * mm, "end": v(0, 6) * mm});
            skLineSegment(sketch, "E91", {"start": v(0, 6) * mm, "end": v(6, 6) * mm});
            skLineSegment(sketch, "E92", {"start": v(6, 6) * mm, "end": v(6, -6) * mm});
            skLineSegment(sketch, "E93", {"start": v(6, -6) * mm, "end": v(0, -6) * mm});
            skLineSegment(sketch, "E94", {"start": v(0, -6) * mm, "end": v(0, 6) * mm});
            skSolve(sketch);
        }
        {
            var Q0;
            Q0 = qSketchRegion(id + "F38", true);
            extrude(context, id + "F39", {"entities" : qUnion([Q0]), "depth" : 25 * mm});
        }
        {
            var Q0;
            Q0=makeQuery(id+"F37.opExtrude","SWEPT_BODY",BODY,{"disambiguationData":[OSD([sQuery(id+"F36.wireOp",EDGE,"E89")])]});
            var Q1;
            Q1=makeQuery(id+"F37.opExtrude","SWEPT_BODY",BODY,{"disambiguationData":[OSD([sQuery(id+"F36.wireOp",EDGE,"E88")])]});
            var Q2;
            Q2=makeQuery(id+"F39.opExtrude","SWEPT_BODY",BODY,{"disambiguationData":[OSD([sQuery(id+"F38.wireOp",EDGE,"E91"),sQuery(id+"F38.wireOp",EDGE,"E92"),sQuery(id+"F38.wireOp",EDGE,"E93"),sQuery(id+"F38.wireOp",EDGE,"E94")])]});
            booleanBodies(context, id + "F40", {"operationType" : BooleanOperationType.SUBTRACTION, "tools" : qUnion([Q0, Q1]), "targets" : qUnion([Q2])});
        }
        {
            var Q0;
            Q0=makeQuery(id+"F39.opExtrude","CAP_EDGE",EDGE,{"disambiguationData":[OSD([sQuery(id+"F38.wireOp",EDGE,"E93")])],"isStart":false});
            var Q1;
            Q1=makeQuery(id+"F39.opExtrude","SWEPT_EDGE",EDGE,{"disambiguationData":[OSD([sQuery(id+"F38.wireOp",EDGE,"E92"),sQuery(id+"F38.wireOp",EDGE,"E93")])]});
            var Q2;
            Q2=makeQuery(id+"F39.opExtrude","CAP_EDGE",EDGE,{"disambiguationData":[OSD([sQuery(id+"F38.wireOp",EDGE,"E92")])],"isStart":false});
            var Q3;
            Q3=makeQuery(id+"F39.opExtrude","CAP_EDGE",EDGE,{"disambiguationData":[OSD([sQuery(id+"F38.wireOp",EDGE,"E91")])],"isStart":false});
            var Q4;
            Q4=makeQuery(id+"F39.opExtrude","SWEPT_EDGE",EDGE,{"disambiguationData":[OSD([sQuery(id+"F38.wireOp",EDGE,"E91"),sQuery(id+"F38.wireOp",EDGE,"E92")])]});
            fillet(context, id + "F41", {"entities" : qUnion([Q0, Q1, Q2, Q3, Q4]), "radius" : 1.5 * mm, "tangentPropagation" : true, "allowEdgeOverflow" : false});
        }
        {
            var Q0;
            Q0=qCreatedBy(makeId("Top.planeOp"),FACE);
            var sketch = newSketch(context, id + "F42", { "sketchPlane" : qUnion([Q0])});
            skLineSegment(sketch, "E95", {"start": v(0, 0) * mm, "end": v(0, 6) * mm});
            skLineSegment(sketch, "E96", {"start": v(0, 6) * mm, "end": v(-6, 6) * mm});
            skLineSegment(sketch, "E97", {"start": v(-6, 6) * mm, "end": v(-6, -6) * mm});
            skLineSegment(sketch, "E98", {"start": v(-6, -6) * mm, "end": v(0, -6) * mm});
            skLineSegment(sketch, "E99", {"start": v(0, -6) * mm, "end": v(0, 0) * mm});
            skSolve(sketch);
        }
        {
            var Q0;
            Q0 = qSketchRegion(id + "F42", true);
            extrude(context, id + "F43", {"entities" : qUnion([Q0]), "depth" : 25 * mm});
        }
        {
            var Q0;
            Q0=makeQuery(id+"F43.opExtrude","SWEPT_BODY",BODY,{"disambiguationData":[OSD([sQuery(id+"F42.wireOp",EDGE,"E95"),sQuery(id+"F42.wireOp",EDGE,"E96"),sQuery(id+"F42.wireOp",EDGE,"E97"),sQuery(id+"F42.wireOp",EDGE,"E98"),sQuery(id+"F42.wireOp",EDGE,"E99")])]});
            transform(context, id + "F44", {"entities" : qUnion([Q0]), "transformType" : TransformType.TRANSLATION_3D, "dx" : 0 * mm, "dy" : 0 * mm, "dz" : 10 * mm, "makeCopy" : false});
        }
        {
            var Q0;
            Q0=makeQuery(id+"F43.opExtrude","SWEPT_BODY",BODY,{"disambiguationData":[OSD([sQuery(id+"F42.wireOp",EDGE,"E95"),sQuery(id+"F42.wireOp",EDGE,"E96"),sQuery(id+"F42.wireOp",EDGE,"E97"),sQuery(id+"F42.wireOp",EDGE,"E98"),sQuery(id+"F42.wireOp",EDGE,"E99")])]});
            var Q1;
            Q1=makeQuery(id+"F1.opExtrude","SWEPT_BODY",BODY,{"disambiguationData":[OSD([sQuery(id+"F0.wireOp",EDGE,"E0.top"),sQuery(id+"F0.wireOp",EDGE,"E1"),sQuery(id+"F0.wireOp",EDGE,"E2"),sQuery(id+"F0.wireOp",EDGE,"E4"),sQuery(id+"F0.wireOp",EDGE,"E5"),sQuery(id+"F0.wireOp",EDGE,"E6"),sQuery(id+"F0.wireOp",EDGE,"E7"),sQuery(id+"F0.wireOp",EDGE,"E8"),sQuery(id+"F0.wireOp",EDGE,"E9"),sQuery(id+"F0.wireOp",EDGE,"E10"),sQuery(id+"F0.wireOp",EDGE,"E11"),sQuery(id+"F0.wireOp",EDGE,"E12.trimOffspring"),sQuery(id+"F0.wireOp",EDGE,"E13"),sQuery(id+"F0.wireOp",EDGE,"E14.trimOffspring"),sQuery(id+"F0.wireOp",EDGE,"E15"),sQuery(id+"F0.wireOp",EDGE,"E16"),sQuery(id+"F0.wireOp",EDGE,"E17")])]});
            booleanBodies(context, id + "F45", {"operationType" : BooleanOperationType.SUBTRACTION, "tools" : qUnion([Q0]), "targets" : qUnion([Q1])});
        }
    });
